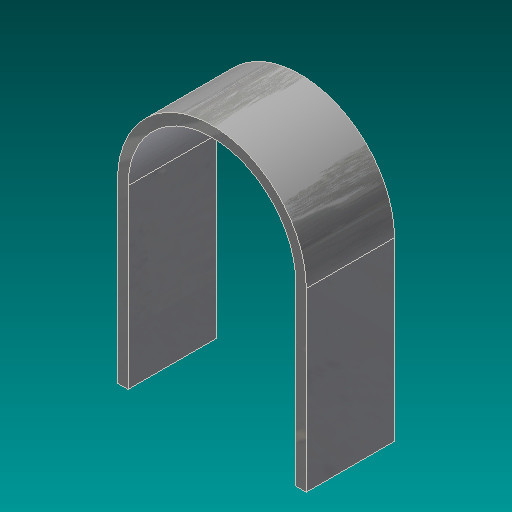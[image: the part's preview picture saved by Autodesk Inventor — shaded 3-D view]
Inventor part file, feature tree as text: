
AUTODESK INVENTOR PART (.ipt)
format: ipt  version: 2017 (Build 210142000, 142)  size: 164,864 bytes
history: native  units: in
note: dims shown in document units (in); Inventor stores cm internally (conversion verified against a paired STEP export)
features: extrude x1, sketch x1, other x1
ambient origin geometry x8: Origin, YZ Plane, XZ Plane, XY Plane, X Axis, Y Axis, Z Axis, Center Point
bodies: Solid1 (feature_tree)
feature tree (3):
  extrude  "Extrusion1"  Depth=0.12in
  sketch  "Sketch1"  dims[d0=1.9in d1=0.12in d2=2.0in d3=1.0in d4=0.0in]
  other  "Definition1"
